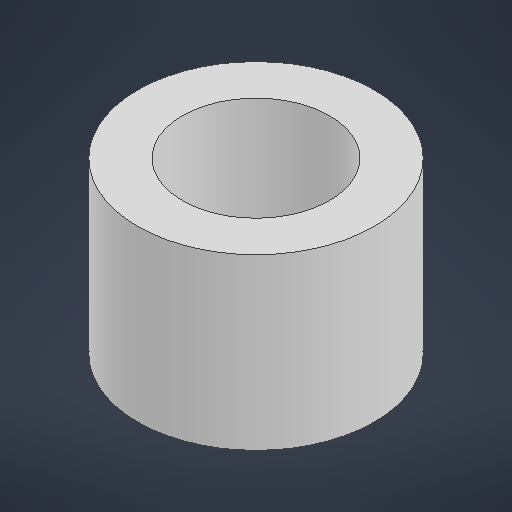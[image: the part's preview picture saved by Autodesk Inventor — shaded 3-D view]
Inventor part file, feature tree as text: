
AUTODESK INVENTOR PART (.ipt)
format: ipt  version: 2025.1 (Build 291241000, 241)  size: 389,632 bytes
history: native  units: mm
features: extrude x1, sketch x1
ambient origin geometry x8: Origin, YZ Plane, XZ Plane, XY Plane, X Axis, Y Axis, Z Axis, Center Point
bodies: Solid1 (feature_tree)
feature tree (2):
  extrude  "Extrusion1"  Depth=6.45mm
  sketch  "Sketch1"  dims[d1=5.6mm d2=9.0mm d3=6.45mm d4=0.0mm]
